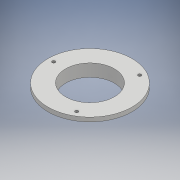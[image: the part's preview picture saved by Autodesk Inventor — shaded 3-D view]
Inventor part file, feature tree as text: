
AUTODESK INVENTOR PART (.ipt)
format: ipt  version: 2018 (Build 220112000, 112)  size: 133,632 bytes
history: native  units: mm
features: other x3, extrude x3, sketch x2, projected_geometry x1
ambient origin geometry x8: Origin, YZ Plane, XZ Plane, XY Plane, X Axis, Y Axis, Z Axis, Center Point
bodies: Solid1 (feature_tree)
feature tree (9):
  other  "Table"
  other  "ACO.RODA25-01"
  other  "ACO.RODA25-02"
  sketch  "Sketch1"  dims[d0=47.0mm d3=4.0mm d4=0.0mm]
  extrude  "Extrusion1"  Depth=4.0mm TaperAngle=0.0deg
  extrude  "Extrusion2"  Depth=12.0mm
  extrude  "Extrusion3"  Depth=12.0mm TaperAngle=360.0deg
  sketch  "Sketch2"  dims[d5=12.0mm d6=0.0mm d8=35.0mm d9=3.0mm d11=360.0deg d13=12.0mm d14=0.0mm d15=81.0mm d17=51.0mm d18=3.0mm]
  projected_geometry  "Projected Loop1"
